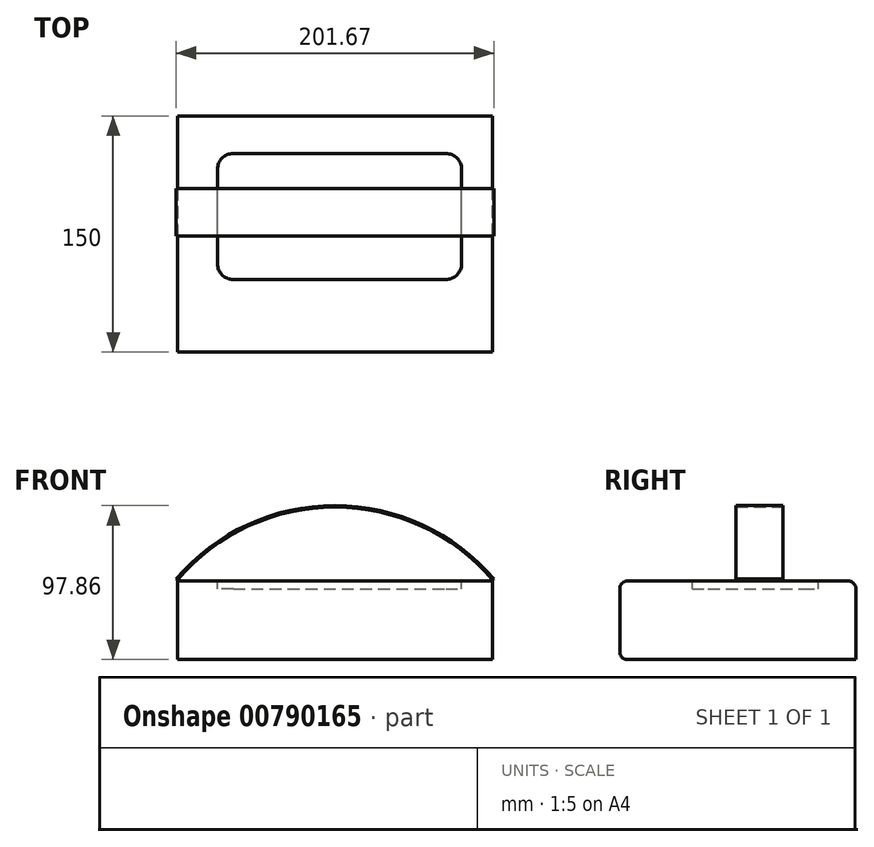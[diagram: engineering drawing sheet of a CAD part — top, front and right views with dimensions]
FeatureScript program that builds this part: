
annotation { "Feature Type Name" : "Feature", "Feature Type Description" : "" }
export const myFeature = defineFeature(function(context is Context, id is Id, definition is map)
    precondition{}
    {
        {
            var Q0;
            Q0=qCreatedBy(makeId("Right.planeOp"),FACE);
            var sketch = newSketch(context, id + "F0", { "sketchPlane" : qUnion([Q0])});
            skLineSegment(sketch, "E0.top", {"start": v(-18.8, -18.04) * mm, "end": v(126.2, -18.04) * mm});
            skLineSegment(sketch, "E0.right", {"start": v(126.2, 26.96) * mm, "end": v(126.2, -18.04) * mm});
            skPoint(sketch, "E1.visualSharp", {"position": v(11.2, 31.96) * mm});
            skPoint(sketch, "E2.visualSharp", {"position": v(-23.8, -3.04) * mm});
            skPoint(sketch, "E3.visualSharp", {"position": v(-23.8, -18.04) * mm});
            skArc(sketch, "E3.filletArc", {"start": v(-23.8, -13.04) * mm, "mid": v(-22.34, -16.57) * mm, "end": v(-18.8, -18.04) * mm});
            skPoint(sketch, "E4.visualSharp", {"position": v(126.2, 31.96) * mm});
            skArc(sketch, "E4.filletArc", {"start": v(126.2, 26.96) * mm, "mid": v(124.73, 30.5) * mm, "end": v(121.2, 31.96) * mm});
            skLineSegment(sketch, "E5", {"start": v(-23.8, 26.96) * mm, "end": v(-23.8, -13.04) * mm});
            skLineSegment(sketch, "E6", {"start": v(121.2, 31.96) * mm, "end": v(-18.8, 31.96) * mm});
            skPoint(sketch, "E7.orphan", {"position": v(-23.8, 47.6) * mm});
            skPoint(sketch, "E8.visualSharp", {"position": v(-23.8, 31.96) * mm});
            skArc(sketch, "E8.filletArc", {"start": v(-18.8, 31.96) * mm, "mid": v(-22.34, 30.5) * mm, "end": v(-23.8, 26.96) * mm});
            skSolve(sketch);
        }
        {
            var Q0;
            Q0=makeQuery(id+"F0.imprint","IMPRINT",FACE,{"disambiguationData":[TD([[makeQuery(id+"F0.imprint","IMPRINT",EDGE,{"derivedFrom":sQuery(id+"F0.wireOp",EDGE,"E0.top")}),1.0]])]});
            extrude(context, id + "F1", {"entities" : qUnion([Q0]), "depth" : 200 * mm, "offsetDistance" : 25 * mm});
        }
        {
            var Q0;
            Q0=makeQuery(id+"F1.opExtrude","SWEPT_FACE",FACE,{"disambiguationData":[OSD([sQuery(id+"F0.wireOp",EDGE,"E6")])]});
            var sketch = newSketch(context, id + "F2", { "sketchPlane" : qUnion([Q0])});
            skLineSegment(sketch, "E9.bottom", {"start": v(35.45, 22.28) * mm, "end": v(170.45, 22.28) * mm});
            skLineSegment(sketch, "E9.top", {"start": v(35.45, 102.28) * mm, "end": v(170.45, 102.28) * mm});
            skLineSegment(sketch, "E9.left", {"start": v(25.45, 32.28) * mm, "end": v(25.45, 92.28) * mm});
            skLineSegment(sketch, "E9.right", {"start": v(180.45, 32.28) * mm, "end": v(180.45, 92.28) * mm});
            skPoint(sketch, "E10.visualSharp", {"position": v(180.45, 22.28) * mm});
            skArc(sketch, "E10.filletArc", {"start": v(170.45, 22.28) * mm, "mid": v(177.53, 25.2) * mm, "end": v(180.45, 32.28) * mm});
            skPoint(sketch, "E11.visualSharp", {"position": v(180.45, 102.28) * mm});
            skArc(sketch, "E11.filletArc", {"start": v(180.45, 92.28) * mm, "mid": v(177.53, 99.35) * mm, "end": v(170.45, 102.28) * mm});
            skPoint(sketch, "E12.visualSharp", {"position": v(25.45, 22.28) * mm});
            skArc(sketch, "E12.filletArc", {"start": v(25.45, 32.28) * mm, "mid": v(28.38, 25.2) * mm, "end": v(35.45, 22.28) * mm});
            skPoint(sketch, "E13.visualSharp", {"position": v(25.45, 102.28) * mm});
            skArc(sketch, "E13.filletArc", {"start": v(35.45, 102.28) * mm, "mid": v(28.38, 99.35) * mm, "end": v(25.45, 92.28) * mm});
            skSolve(sketch);
        }
        {
            var Q0;
            Q0 = qSketchRegion(id + "F2", true);
            extrude(context, id + "F3", {"entities" : qUnion([Q0]), "operationType" : NewBodyOperationType.REMOVE, "oppositeDirection" : true, "depth" : 5 * mm, "offsetDistance" : 25 * mm});
        }
        {
            var Q0;
            Q0=qCreatedBy(makeId("Front.planeOp"),FACE);
            cPlane(context, id + "F4", {"entities" : qUnion([Q0]), "cplaneType" : CPlaneType.OFFSET, "offset" : 65 * mm, "oppositeDirection" : true, "width" : 150 * mm, "height" : 150 * mm});
        }
        {
            var Q0;
            Q0=qCreatedBy(id+"F4.planeOp",FACE);
            var sketch = newSketch(context, id + "F5", { "sketchPlane" : qUnion([Q0])});
            skArc(sketch, "E14", {"start": v(0, 32.6) * mm, "mid": v(100.1, 78.82) * mm, "end": v(200.15, 32.52) * mm});
            skArc(sketch, "E15.0", {"start": v(-0.76, 33.25) * mm, "mid": v(100.1, 79.82) * mm, "end": v(200.9, 33.17) * mm});
            skLineSegment(sketch, "E16", {"start": v(-0.76, 33.25) * mm, "end": v(0, 32.6) * mm});
            skLineSegment(sketch, "E17", {"start": v(200.9, 33.17) * mm, "end": v(200.15, 32.52) * mm});
            skSolve(sketch);
        }
        {
            var Q0;
            Q0 = qSketchRegion(id + "F5", true);
            extrude(context, id + "F6", {"entities" : qUnion([Q0]), "depth" : 30 * mm, "offsetDistance" : 25 * mm, "symmetric" : true});
        }
    });
